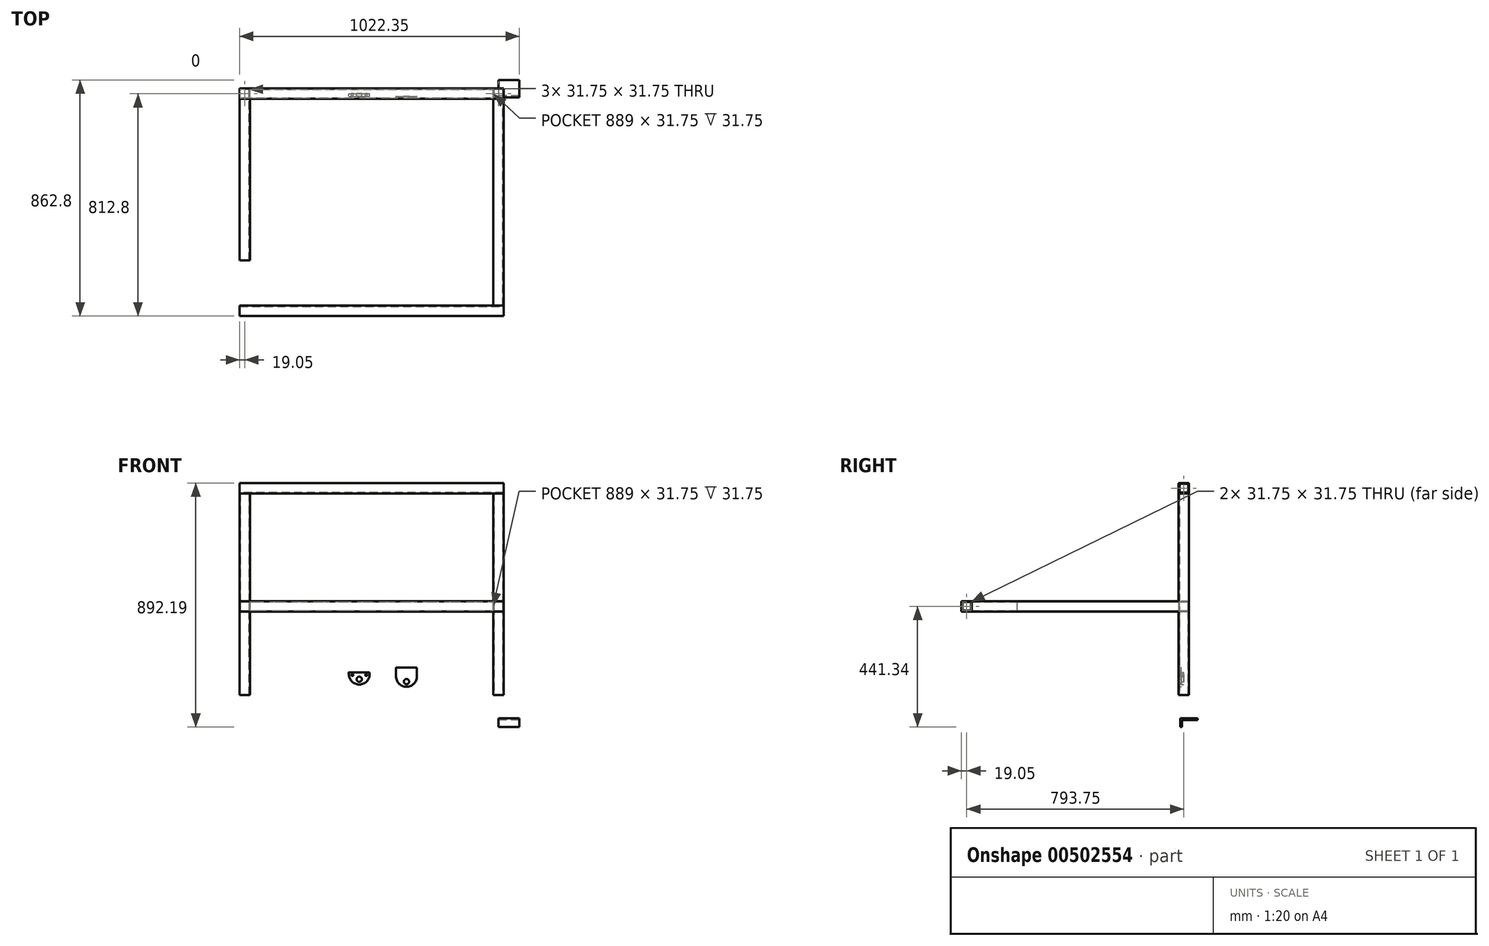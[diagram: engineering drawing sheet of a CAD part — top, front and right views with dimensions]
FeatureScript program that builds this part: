
annotation { "Feature Type Name" : "Feature", "Feature Type Description" : "" }
export const myFeature = defineFeature(function(context is Context, id is Id, definition is map)
    precondition{}
    {
        {
            var Q0;
            Q0=qCreatedBy(makeId("Top.planeOp"),FACE);
            var sketch = newSketch(context, id + "F0", { "sketchPlane" : qUnion([Q0])});
            skLineSegment(sketch, "E0.bottom", {"start": v(19.05, -19.05) * mm, "end": v(-19.05, -19.05) * mm});
            skLineSegment(sketch, "E0.top", {"start": v(19.05, 19.05) * mm, "end": v(-19.05, 19.05) * mm});
            skLineSegment(sketch, "E0.left", {"start": v(19.05, -19.05) * mm, "end": v(19.05, 19.05) * mm});
            skLineSegment(sketch, "E0.right", {"start": v(-19.05, -19.05) * mm, "end": v(-19.05, 19.05) * mm});
            skPoint(sketch, "E0.middle", {"position": v(0, 0) * mm});
            skLineSegment(sketch, "E1.bottom", {"start": v(15.88, 15.88) * mm, "end": v(-15.88, 15.87) * mm});
            skLineSegment(sketch, "E1.top", {"start": v(15.88, -15.87) * mm, "end": v(-15.88, -15.88) * mm});
            skLineSegment(sketch, "E1.left", {"start": v(15.88, 15.88) * mm, "end": v(15.88, -15.87) * mm});
            skLineSegment(sketch, "E1.right", {"start": v(-15.88, 15.87) * mm, "end": v(-15.88, -15.88) * mm});
            skSolve(sketch);
        }
        {
            var Q0;
            Q0=makeQuery(id+"F0.imprint","IMPRINT",FACE,{"disambiguationData":[TD([[makeQuery(id+"F0.imprint","IMPRINT",EDGE,{"derivedFrom":sQuery(id+"F0.wireOp",EDGE,"E0.bottom")}),-1.0]])]});
            extrude(context, id + "F1", {"entities" : qUnion([Q0]), "depth" : 342.9 * mm});
        }
        {
            var Q0;
            Q0=makeQuery(id+"F1.opExtrude","SWEPT_FACE",FACE,{"disambiguationData":[OSD([sQuery(id+"F0.wireOp",EDGE,"E0.right")])]});
            var sketch = newSketch(context, id + "F2", { "sketchPlane" : qUnion([Q0])});
            skLineSegment(sketch, "E2.bottom", {"start": v(-19.05, 342.9) * mm, "end": v(19.05, 342.9) * mm});
            skLineSegment(sketch, "E2.top", {"start": v(-19.05, 304.8) * mm, "end": v(19.05, 304.8) * mm});
            skLineSegment(sketch, "E2.left", {"start": v(-19.05, 342.9) * mm, "end": v(-19.05, 304.8) * mm});
            skLineSegment(sketch, "E2.right", {"start": v(19.05, 342.9) * mm, "end": v(19.05, 304.8) * mm});
            skLineSegment(sketch, "E3.bottom", {"start": v(15.87, 307.98) * mm, "end": v(-15.87, 307.98) * mm});
            skLineSegment(sketch, "E3.top", {"start": v(15.87, 339.73) * mm, "end": v(-15.87, 339.73) * mm});
            skLineSegment(sketch, "E3.left", {"start": v(15.88, 307.98) * mm, "end": v(15.88, 339.73) * mm});
            skLineSegment(sketch, "E3.right", {"start": v(-15.87, 307.98) * mm, "end": v(-15.87, 339.73) * mm});
            skPoint(sketch, "E3.middle", {"position": v(0, 323.85) * mm});
            skSolve(sketch);
        }
        {
            var Q0;
            Q0 = qSketchRegion(id + "F2", true);
            extrude(context, id + "F3", {"entities" : qUnion([Q0]), "operationType" : NewBodyOperationType.ADD, "depth" : 889 * mm});
        }
        {
            var Q0;
            Q0=makeQuery(id+"F3.opExtrude","SWEPT_FACE",FACE,{"disambiguationData":[OSD([sQuery(id+"F2.wireOp",EDGE,"E2.top")])]});
            var sketch = newSketch(context, id + "F4", { "sketchPlane" : qUnion([Q0])});
            skLineSegment(sketch, "E4.bottom", {"start": v(-908.05, 19.05) * mm, "end": v(-946.15, 19.05) * mm});
            skLineSegment(sketch, "E4.top", {"start": v(-908.05, -19.05) * mm, "end": v(-946.15, -19.05) * mm});
            skLineSegment(sketch, "E4.left", {"start": v(-908.05, 19.05) * mm, "end": v(-908.05, -19.05) * mm});
            skLineSegment(sketch, "E4.right", {"start": v(-946.15, 19.05) * mm, "end": v(-946.15, -19.05) * mm});
            skLineSegment(sketch, "E5.bottom", {"start": v(-911.23, 15.87) * mm, "end": v(-942.98, 15.87) * mm});
            skLineSegment(sketch, "E5.top", {"start": v(-911.23, -15.88) * mm, "end": v(-942.98, -15.88) * mm});
            skLineSegment(sketch, "E5.left", {"start": v(-911.23, 15.87) * mm, "end": v(-911.23, -15.87) * mm});
            skLineSegment(sketch, "E5.right", {"start": v(-942.98, 15.87) * mm, "end": v(-942.98, -15.87) * mm});
            skPoint(sketch, "E5.middle", {"position": v(-927.1, 0) * mm});
            skSolve(sketch);
        }
        {
            var Q0;
            Q0=makeQuery(id+"F4.imprint","IMPRINT",FACE,{"disambiguationData":[TD([[makeQuery(id+"F4.imprint","IMPRINT",EDGE,{"derivedFrom":sQuery(id+"F4.wireOp",EDGE,"E4.bottom")}),1.0]])]});
            extrude(context, id + "F5", {"entities" : qUnion([Q0]), "depth" : 304.8 * mm});
        }
        {
            var Q0;
            Q0=makeQuery(id+"F5.opExtrude","CAP_FACE",FACE,{"disambiguationData":[OSD([sQuery(id+"F4.wireOp",EDGE,"E4.bottom"),sQuery(id+"F4.wireOp",EDGE,"E4.top"),sQuery(id+"F4.wireOp",EDGE,"E4.left"),sQuery(id+"F4.wireOp",EDGE,"E4.right"),sQuery(id+"F4.wireOp",EDGE,"E5.bottom"),sQuery(id+"F4.wireOp",EDGE,"E5.top"),sQuery(id+"F4.wireOp",EDGE,"E5.left"),sQuery(id+"F4.wireOp",EDGE,"E5.right")])],"isStart":true});
            extrude(context, id + "F6", {"entities" : qUnion([Q0]), "depth" : 38.1 * mm});
        }
        {
            var Q0;
            Q0=makeQuery(id+"F6.opExtrude","CAP_FACE",FACE,{"disambiguationData":[OSD([sQuery(id+"F4.wireOp",EDGE,"E4.bottom"),sQuery(id+"F4.wireOp",EDGE,"E4.top"),sQuery(id+"F4.wireOp",EDGE,"E4.left"),sQuery(id+"F4.wireOp",EDGE,"E4.right"),sQuery(id+"F4.wireOp",EDGE,"E5.bottom"),sQuery(id+"F4.wireOp",EDGE,"E5.top"),sQuery(id+"F4.wireOp",EDGE,"E5.left"),sQuery(id+"F4.wireOp",EDGE,"E5.right")])],"isStart":false});
            extrude(context, id + "F7", {"entities" : qUnion([Q0]), "operationType" : NewBodyOperationType.ADD, "depth" : 393.7 * mm});
        }
        {
            var Q0;
            Q0=makeQuery(id+"F3.boolean.opBoolean","MERGE",FACE,{"derivedFrom":[makeQuery(id+"F1.opExtrude","CAP_FACE",FACE,{"disambiguationData":[OSD([sQuery(id+"F0.wireOp",EDGE,"E0.bottom"),sQuery(id+"F0.wireOp",EDGE,"E0.top"),sQuery(id+"F0.wireOp",EDGE,"E0.left"),sQuery(id+"F0.wireOp",EDGE,"E0.right"),sQuery(id+"F0.wireOp",EDGE,"E1.bottom"),sQuery(id+"F0.wireOp",EDGE,"E1.top"),sQuery(id+"F0.wireOp",EDGE,"E1.left"),sQuery(id+"F0.wireOp",EDGE,"E1.right")])],"isStart":false}),makeQuery(id+"F3.opExtrude","SWEPT_FACE",FACE,{"disambiguationData":[OSD([sQuery(id+"F2.wireOp",EDGE,"E2.bottom")])]})]});
            var sketch = newSketch(context, id + "F8", { "sketchPlane" : qUnion([Q0])});
            skLineSegment(sketch, "E6.bottom", {"start": v(19.05, 19.05) * mm, "end": v(-19.05, 19.05) * mm});
            skLineSegment(sketch, "E6.top", {"start": v(19.05, -19.05) * mm, "end": v(-19.05, -19.05) * mm});
            skLineSegment(sketch, "E6.left", {"start": v(19.05, 19.05) * mm, "end": v(19.05, -19.05) * mm});
            skLineSegment(sketch, "E6.right", {"start": v(-19.05, 19.05) * mm, "end": v(-19.05, -19.05) * mm});
            skSolve(sketch);
        }
        {
            var Q0;
            Q0=makeQuery(id+"F8.imprint","IMPRINT",FACE,{"disambiguationData":[TD([[makeQuery(id+"F8.imprint","IMPRINT",EDGE,{"derivedFrom":sQuery(id+"F8.wireOp",EDGE,"E6.bottom")}),1.0]])]});
            extrude(context, id + "F9", {"entities" : qUnion([Q0]), "operationType" : NewBodyOperationType.ADD, "depth" : 393.7 * mm});
        }
        {
            var Q0;
            {var subQ0=sQuery(id+"F4.wireOp",EDGE,"E4.right");Q0=makeQuery(id+"F7.boolean.opBoolean","MERGE",FACE,{"derivedFrom":[makeQuery(id+"F6.opExtrude","SWEPT_FACE",FACE,{"disambiguationData":[OSD([subQ0])]}),makeQuery(id+"F7.opExtrude","SWEPT_FACE",FACE,{"disambiguationData":[OSD([subQ0])]})]});}
            var sketch = newSketch(context, id + "F10", { "sketchPlane" : qUnion([Q0])});
            skLineSegment(sketch, "E7.bottom", {"start": v(-19.05, 736.6) * mm, "end": v(19.05, 736.6) * mm});
            skLineSegment(sketch, "E7.top", {"start": v(-19.05, 774.7) * mm, "end": v(19.05, 774.7) * mm});
            skLineSegment(sketch, "E7.left", {"start": v(-19.05, 736.6) * mm, "end": v(-19.05, 774.7) * mm});
            skLineSegment(sketch, "E7.right", {"start": v(19.05, 736.6) * mm, "end": v(19.05, 774.7) * mm});
            skLineSegment(sketch, "E8.bottom", {"start": v(15.88, 739.78) * mm, "end": v(-15.88, 739.78) * mm});
            skLineSegment(sketch, "E8.top", {"start": v(15.88, 771.53) * mm, "end": v(-15.88, 771.53) * mm});
            skLineSegment(sketch, "E8.left", {"start": v(15.87, 739.78) * mm, "end": v(15.87, 771.53) * mm});
            skLineSegment(sketch, "E8.right", {"start": v(-15.88, 739.78) * mm, "end": v(-15.88, 771.53) * mm});
            skPoint(sketch, "E8.middle", {"position": v(0, 755.65) * mm});
            skSolve(sketch);
        }
        {
            var Q0;
            Q0=makeQuery(id+"F10.imprint","IMPRINT",FACE,{"disambiguationData":[TD([[makeQuery(id+"F10.imprint","IMPRINT",EDGE,{"derivedFrom":sQuery(id+"F10.wireOp",EDGE,"E7.bottom")}),-1.0]])]});
            extrude(context, id + "F11", {"entities" : qUnion([Q0]), "oppositeDirection" : true, "depth" : 965.2 * mm});
        }
        {
            var Q0;
            Q0=makeQuery(id+"F9.boolean.opBoolean","MERGE",FACE,{"derivedFrom":[makeQuery(id+"F3.boolean.opBoolean","MERGE",FACE,{"derivedFrom":[makeQuery(id+"F1.opExtrude","SWEPT_FACE",FACE,{"disambiguationData":[OSD([sQuery(id+"F0.wireOp",EDGE,"E0.bottom")])]}),makeQuery(id+"F3.opExtrude","SWEPT_FACE",FACE,{"disambiguationData":[OSD([sQuery(id+"F2.wireOp",EDGE,"E2.right")])]})]}),makeQuery(id+"F9.opExtrude","SWEPT_FACE",FACE,{"disambiguationData":[OSD([sQuery(id+"F8.wireOp",EDGE,"E6.top")])]})]});
            var sketch = newSketch(context, id + "F12", { "sketchPlane" : qUnion([Q0])});
            skLineSegment(sketch, "E9", {"start": v(-19.05, 342.9) * mm, "end": v(-19.05, 304.8) * mm});
            skLineSegment(sketch, "E10.bottom", {"start": v(-908.05, 342.9) * mm, "end": v(-946.15, 342.9) * mm});
            skLineSegment(sketch, "E10.top", {"start": v(-908.05, 304.7) * mm, "end": v(-946.15, 304.7) * mm});
            skLineSegment(sketch, "E10.left", {"start": v(-908.05, 342.9) * mm, "end": v(-908.05, 304.7) * mm});
            skLineSegment(sketch, "E10.right", {"start": v(-946.15, 342.9) * mm, "end": v(-946.15, 304.7) * mm});
            skLineSegment(sketch, "E11.bottom", {"start": v(-942.98, 339.62) * mm, "end": v(-911.23, 339.62) * mm});
            skLineSegment(sketch, "E11.top", {"start": v(-942.98, 307.87) * mm, "end": v(-911.23, 307.87) * mm});
            skLineSegment(sketch, "E11.left", {"start": v(-942.98, 339.62) * mm, "end": v(-942.98, 307.87) * mm});
            skLineSegment(sketch, "E11.right", {"start": v(-911.23, 339.62) * mm, "end": v(-911.23, 307.87) * mm});
            skPoint(sketch, "E11.middle", {"position": v(-927.1, 323.75) * mm});
            skSolve(sketch);
        }
        {
            var Q0;
            {var subQ5=sQuery(id+"F12.wireOp",EDGE,"E10.bottom");Q0=makeQuery(id+"F12.imprint","IMPRINT",FACE,{"disambiguationData":[TD([[makeQuery(id+"F12.imprint","IMPRINT",EDGE,{"derivedFrom":subQ5}),1.0]])]});}
            extrude(context, id + "F13", {"entities" : qUnion([Q0]), "depth" : 590.55 * mm, "offsetDistance" : 25.4 * mm});
        }
        {
            var Q0;
            Q0=makeQuery(id+"F9.boolean.opBoolean","MERGE",FACE,{"derivedFrom":[makeQuery(id+"F3.boolean.opBoolean","MERGE",FACE,{"derivedFrom":[makeQuery(id+"F1.opExtrude","SWEPT_FACE",FACE,{"disambiguationData":[OSD([sQuery(id+"F0.wireOp",EDGE,"E0.bottom")])]}),makeQuery(id+"F3.opExtrude","SWEPT_FACE",FACE,{"disambiguationData":[OSD([sQuery(id+"F2.wireOp",EDGE,"E2.right")])]})]}),makeQuery(id+"F9.opExtrude","SWEPT_FACE",FACE,{"disambiguationData":[OSD([sQuery(id+"F8.wireOp",EDGE,"E6.top")])]})]});
            var sketch = newSketch(context, id + "F14", { "sketchPlane" : qUnion([Q0])});
            skLineSegment(sketch, "E12.bottom", {"start": v(-19.05, 342.9) * mm, "end": v(19.05, 342.9) * mm});
            skLineSegment(sketch, "E12.top", {"start": v(-19.05, 304.8) * mm, "end": v(19.05, 304.8) * mm});
            skLineSegment(sketch, "E12.left", {"start": v(-19.05, 342.9) * mm, "end": v(-19.05, 304.8) * mm});
            skLineSegment(sketch, "E12.right", {"start": v(19.05, 342.9) * mm, "end": v(19.05, 304.8) * mm});
            skLineSegment(sketch, "E13.bottom", {"start": v(-15.88, 339.73) * mm, "end": v(15.87, 339.73) * mm});
            skLineSegment(sketch, "E13.top", {"start": v(-15.88, 307.98) * mm, "end": v(15.87, 307.98) * mm});
            skLineSegment(sketch, "E13.left", {"start": v(-15.88, 339.73) * mm, "end": v(-15.88, 307.98) * mm});
            skLineSegment(sketch, "E13.right", {"start": v(15.87, 339.73) * mm, "end": v(15.87, 307.98) * mm});
            skPoint(sketch, "E13.middle", {"position": v(0, 323.85) * mm});
            skPoint(sketch, "E13.middle.positionSnap0", {"position": v(19.05, 323.85) * mm});
            skPoint(sketch, "E13.centerSnap0", {"position": v(19.05, 323.85) * mm});
            skSolve(sketch);
        }
        {
            var Q0;
            Q0=makeQuery(id+"F14.imprint","IMPRINT",FACE,{"disambiguationData":[TD([[makeQuery(id+"F14.imprint","IMPRINT",EDGE,{"derivedFrom":sQuery(id+"F14.wireOp",EDGE,"E12.bottom")}),-1.0]])]});
            extrude(context, id + "F15", {"entities" : qUnion([Q0]), "operationType" : NewBodyOperationType.ADD, "depth" : 755.65 * mm});
        }
        {
            var Q0;
            Q0=qCreatedBy(makeId("Right.planeOp"),FACE);
            var sketch = newSketch(context, id + "F16", { "sketchPlane" : qUnion([Q0])});
            skLineSegment(sketch, "E14", {"start": v(50, -85.74) * mm, "end": v(-13.5, -85.74) * mm});
            skLineSegment(sketch, "E15", {"start": v(-13.5, -85.74) * mm, "end": v(-13.5, -117.5) * mm});
            skLineSegment(sketch, "E16", {"start": v(-13.5, -117.5) * mm, "end": v(-7.15, -117.5) * mm});
            skLineSegment(sketch, "E17", {"start": v(50, -85.74) * mm, "end": v(50, -92.1) * mm});
            skLineSegment(sketch, "E18", {"start": v(50, -92.1) * mm, "end": v(-7.15, -92.1) * mm});
            skLineSegment(sketch, "E19", {"start": v(-7.15, -92.1) * mm, "end": v(-7.15, -117.5) * mm});
            skSolve(sketch);
        }
        {
            var Q0;
            Q0=makeQuery(id+"F16.imprint","IMPRINT",FACE,{"disambiguationData":[TD([[makeQuery(id+"F16.imprint","IMPRINT",EDGE,{"derivedFrom":sQuery(id+"F16.wireOp",EDGE,"E14")}),1.0]])]});
            extrude(context, id + "F17", {"entities" : qUnion([Q0]), "depth" : 76.2 * mm});
        }
        {
            var Q0;
            Q0=qCreatedBy(makeId("Front.planeOp"),FACE);
            var sketch = newSketch(context, id + "F18", { "sketchPlane" : qUnion([Q0])});
            skArc(sketch, "E20", {"start": v(-546.72, 76.13) * mm, "mid": v(-508.62, 38.03) * mm, "end": v(-470.52, 76.13) * mm});
            skCircle(sketch, "E21", {"center": v(-508.82, 57.08) * mm, "radius": 9.53 * mm});
            skLineSegment(sketch, "E22", {"start": v(-483.22, 82.48) * mm, "end": v(-483.22, 72.95) * mm});
            skCircle(sketch, "E23", {"center": v(-534.02, 72.75) * mm, "radius": 3.37 * mm});
            skCircle(sketch, "E24", {"center": v(-483.22, 72.95) * mm, "radius": 3.37 * mm});
            skLineSegment(sketch, "E25", {"start": v(-534.02, 76.13) * mm, "end": v(-534.02, 76.13) * mm});
            skLineSegment(sketch, "E26", {"start": v(-470.52, 76.13) * mm, "end": v(-470.52, 82.48) * mm});
            skLineSegment(sketch, "E27", {"start": v(-546.72, 76.13) * mm, "end": v(-546.72, 82.48) * mm});
            skLineSegment(sketch, "E28", {"start": v(-546.72, 82.48) * mm, "end": v(-470.52, 82.48) * mm});
            skSolve(sketch);
        }
        {
            var Q0;
            {var subQ1=sQuery(id+"F18.wireOp",EDGE,"E20");Q0=makeQuery(id+"F18.imprint","IMPRINT",FACE,{"disambiguationData":[TD([[makeQuery(id+"F18.imprint","IMPRINT",EDGE,{"derivedFrom":subQ1}),1.0]])]});}
            extrude(context, id + "F19", {"entities" : qUnion([Q0]), "depth" : 9.52 * mm});
        }
        {
            var Q0;
            Q0=makeQuery(id+"F19.opExtrude","CAP_EDGE",EDGE,{"disambiguationData":[OSD([sQuery(id+"F18.wireOp",EDGE,"E23")])],"isStart":false});
            var Q1;
            Q1=makeQuery(id+"F19.opExtrude","CAP_EDGE",EDGE,{"disambiguationData":[OSD([sQuery(id+"F18.wireOp",EDGE,"E21")])],"isStart":false});
            var Q2;
            Q2=makeQuery(id+"F19.opExtrude","CAP_EDGE",EDGE,{"disambiguationData":[OSD([sQuery(id+"F18.wireOp",EDGE,"E24")])],"isStart":false});
            var Q3;
            Q3=makeQuery(id+"F19.opExtrude","CAP_EDGE",EDGE,{"disambiguationData":[OSD([sQuery(id+"F18.wireOp",EDGE,"E20")])],"isStart":false});
            var Q4;
            Q4=makeQuery(id+"F19.opExtrude","CAP_EDGE",EDGE,{"disambiguationData":[OSD([sQuery(id+"F18.wireOp",EDGE,"E24")])],"isStart":true});
            var Q5;
            Q5=makeQuery(id+"F19.opExtrude","CAP_EDGE",EDGE,{"disambiguationData":[OSD([sQuery(id+"F18.wireOp",EDGE,"E23")])],"isStart":true});
            var Q6;
            Q6=makeQuery(id+"F19.opExtrude","CAP_EDGE",EDGE,{"disambiguationData":[OSD([sQuery(id+"F18.wireOp",EDGE,"E21")])],"isStart":true});
            var Q7;
            Q7=makeQuery(id+"F19.opExtrude","CAP_EDGE",EDGE,{"disambiguationData":[OSD([sQuery(id+"F18.wireOp",EDGE,"E20")])],"isStart":true});
            fillet(context, id + "F20", {"entities" : qUnion([Q0, Q1, Q2, Q3, Q4, Q5, Q6, Q7]), "radius" : 1.27 * mm, "tangentPropagation" : true, "allowEdgeOverflow" : false});
        }
        {
            var Q0;
            Q0=makeQuery(id+"F19.opExtrude","CAP_FACE",FACE,{"disambiguationData":[OSD([sQuery(id+"F18.wireOp",EDGE,"E20"),sQuery(id+"F18.wireOp",EDGE,"Ygi6MwIS-Yvjz-SSp6-drDn-ZyGcmScmYJQb"),sQuery(id+"F18.wireOp",EDGE,"E21"),sQuery(id+"F18.wireOp",EDGE,"az7XY3kz-kZmA-XSl0-LDq3-UVvBn7PKCw2h"),sQuery(id+"F18.wireOp",EDGE,"U9za1MZr-jVt6-irhi-U4lY-rjCycSk8VeMD"),sQuery(id+"F18.wireOp",EDGE,"E23"),sQuery(id+"F18.wireOp",EDGE,"E24")])],"isStart":false});
            var sketch = newSketch(context, id + "F21", { "sketchPlane" : qUnion([Q0])});
            skArc(sketch, "E29", {"start": v(-374.13, 67.65) * mm, "mid": v(-336.03, 29.55) * mm, "end": v(-297.93, 67.65) * mm});
            skLineSegment(sketch, "E30", {"start": v(-374.13, 67.65) * mm, "end": v(-374.13, 99.4) * mm});
            skLineSegment(sketch, "E31", {"start": v(-297.93, 67.65) * mm, "end": v(-297.93, 99.4) * mm});
            skLineSegment(sketch, "E32", {"start": v(-374.13, 99.4) * mm, "end": v(-297.93, 99.4) * mm});
            skLineSegment(sketch, "E33", {"start": v(-336.03, 29.55) * mm, "end": v(-336.03, 48.6) * mm});
            skCircle(sketch, "E34", {"center": v(-336.03, 48.6) * mm, "radius": 9.53 * mm});
            skSolve(sketch);
        }
        {
            var Q0;
            {var subQ1=sQuery(id+"F21.wireOp",EDGE,"E30");Q0=makeQuery(id+"F21.imprint","IMPRINT",FACE,{"disambiguationData":[TD([[makeQuery(id+"F21.imprint","IMPRINT",EDGE,{"derivedFrom":subQ1}),-1.0]])]});}
            extrude(context, id + "F22", {"entities" : qUnion([Q0]), "depth" : 9.52 * mm});
        }
        {
            var Q0;
            Q0=makeQuery(id+"F22.opExtrude","CAP_EDGE",EDGE,{"disambiguationData":[OSD([sQuery(id+"F21.wireOp",EDGE,"E34")])],"isStart":false});
            var Q1;
            Q1=makeQuery(id+"F22.opExtrude","CAP_EDGE",EDGE,{"disambiguationData":[OSD([sQuery(id+"F21.wireOp",EDGE,"E29")])],"isStart":false});
            var Q2;
            Q2=makeQuery(id+"F22.opExtrude","CAP_EDGE",EDGE,{"disambiguationData":[OSD([sQuery(id+"F21.wireOp",EDGE,"E31")])],"isStart":false});
            var Q3;
            Q3=makeQuery(id+"F22.opExtrude","CAP_EDGE",EDGE,{"disambiguationData":[OSD([sQuery(id+"F21.wireOp",EDGE,"E30")])],"isStart":false});
            var Q4;
            Q4=makeQuery(id+"F22.opExtrude","CAP_EDGE",EDGE,{"disambiguationData":[OSD([sQuery(id+"F21.wireOp",EDGE,"E34")])],"isStart":true});
            var Q5;
            Q5=makeQuery(id+"F22.opExtrude","CAP_EDGE",EDGE,{"disambiguationData":[OSD([sQuery(id+"F21.wireOp",EDGE,"E29")])],"isStart":true});
            var Q6;
            Q6=makeQuery(id+"F22.opExtrude","CAP_EDGE",EDGE,{"disambiguationData":[OSD([sQuery(id+"F21.wireOp",EDGE,"E31")])],"isStart":true});
            var Q7;
            Q7=makeQuery(id+"F22.opExtrude","CAP_EDGE",EDGE,{"disambiguationData":[OSD([sQuery(id+"F21.wireOp",EDGE,"E30")])],"isStart":true});
            fillet(context, id + "F23", {"entities" : qUnion([Q0, Q1, Q2, Q3, Q4, Q5, Q6, Q7]), "radius" : 1.27 * mm, "tangentPropagation" : true, "allowEdgeOverflow" : false});
        }
        {
            var Q0;
            Q0=makeQuery(id+"F15.boolean.opBoolean","MERGE",FACE,{"derivedFrom":[makeQuery(id+"F9.boolean.opBoolean","MERGE",FACE,{"derivedFrom":[makeQuery(id+"F1.opExtrude","SWEPT_FACE",FACE,{"disambiguationData":[OSD([sQuery(id+"F0.wireOp",EDGE,"E0.left")])]}),makeQuery(id+"F9.opExtrude","SWEPT_FACE",FACE,{"disambiguationData":[OSD([sQuery(id+"F8.wireOp",EDGE,"E6.left")])]})]}),makeQuery(id+"F15.opExtrude","SWEPT_FACE",FACE,{"disambiguationData":[OSD([sQuery(id+"F14.wireOp",EDGE,"E12.right")])]})]});
            var sketch = newSketch(context, id + "F24", { "sketchPlane" : qUnion([Q0])});
            skLineSegment(sketch, "E35.bottom", {"start": v(-774.7, 342.9) * mm, "end": v(-812.8, 342.9) * mm});
            skLineSegment(sketch, "E35.top", {"start": v(-774.7, 304.8) * mm, "end": v(-812.8, 304.8) * mm});
            skLineSegment(sketch, "E35.left", {"start": v(-774.7, 342.9) * mm, "end": v(-774.7, 304.8) * mm});
            skLineSegment(sketch, "E35.right", {"start": v(-812.8, 342.9) * mm, "end": v(-812.8, 304.8) * mm});
            skLineSegment(sketch, "E36.bottom", {"start": v(-777.88, 339.72) * mm, "end": v(-809.62, 339.72) * mm});
            skLineSegment(sketch, "E36.top", {"start": v(-777.88, 307.97) * mm, "end": v(-809.62, 307.97) * mm});
            skLineSegment(sketch, "E36.left", {"start": v(-777.88, 339.72) * mm, "end": v(-777.88, 307.97) * mm});
            skLineSegment(sketch, "E36.right", {"start": v(-809.62, 339.72) * mm, "end": v(-809.62, 307.97) * mm});
            skSolve(sketch);
        }
        {
            var Q0;
            Q0=makeQuery(id+"F24.imprint","IMPRINT",FACE,{"disambiguationData":[TD([[makeQuery(id+"F24.imprint","IMPRINT",EDGE,{"derivedFrom":sQuery(id+"F24.wireOp",EDGE,"E35.bottom")}),1.0]])]});
            extrude(context, id + "F25", {"entities" : qUnion([Q0]), "oppositeDirection" : true, "depth" : 965.2 * mm, "offsetDistance" : 25.4 * mm});
        }
    });
